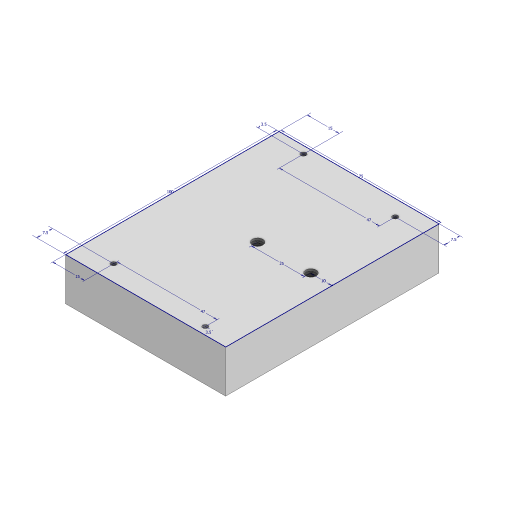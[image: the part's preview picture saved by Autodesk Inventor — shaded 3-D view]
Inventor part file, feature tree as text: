
AUTODESK INVENTOR PART (.ipt)
format: ipt  version: 2023 (Build 270158000, 158)  size: 114,688 bytes
history: native  units: mm
features: hole x2, sketch x1, extrude x1
ambient origin geometry x8: Origin, YZ Plane, XZ Plane, XY Plane, X Axis, Y Axis, Z Axis, Center Point
bodies: Solid1 (feature_tree)
feature tree (4):
  sketch  "Sketch1"  dims[d0=75.0mm d1=100.0mm d2=7.5mm d3=3.5mm d4=3.5mm d5=7.5mm d6=47.0mm d7=47.0mm d8=15.0mm d9=15.0mm d10=25.0mm d11=10.0mm d12=20.0mm d13=0.0mm d14=2.459mm d15=6.0mm d16=4.0mm d17=2.0mm d18=90.0deg d19=8.0mm d20=20.594885mm d21=4.917mm d22=12.0mm d23=4.0mm d24=2.0mm d25=90.0deg d26=16.0mm d27=20.594885mm]
  extrude  "Extrusion1"  Depth=100.0mm
  hole  "Hole1"  [1 undecoded]
  hole  "Hole2"  [1 undecoded]
note: 2 required parameter values undecoded (feature->parameter linkage not recoverable at this tier; creation-order binding heuristic only, values carry confidence <= 0.55)
